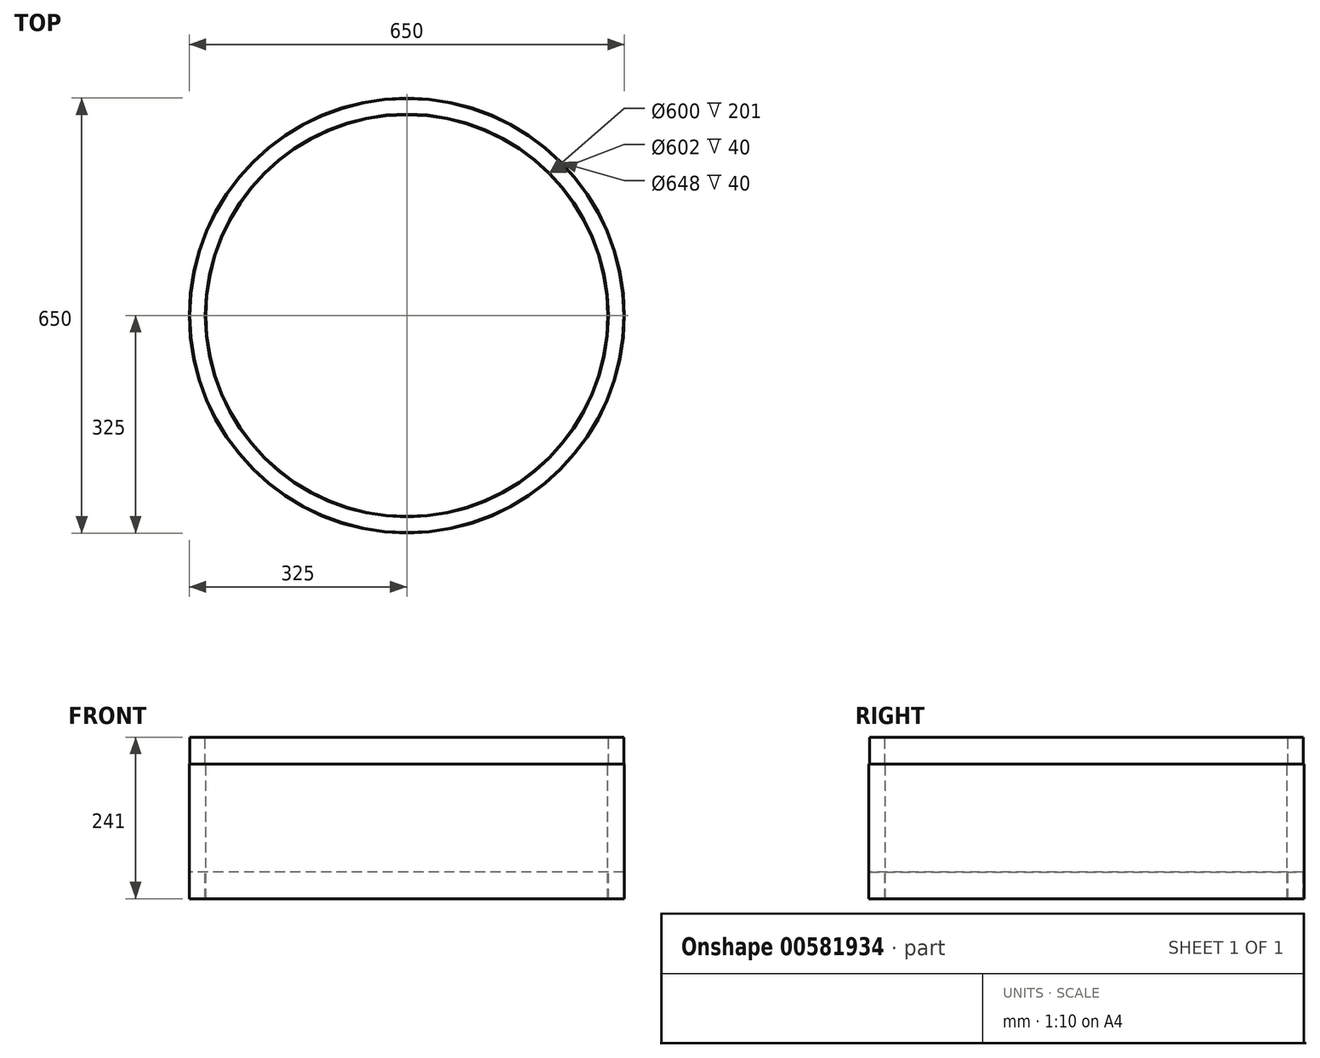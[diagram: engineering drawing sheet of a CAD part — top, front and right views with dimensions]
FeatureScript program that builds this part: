
annotation { "Feature Type Name" : "Feature", "Feature Type Description" : "" }
export const myFeature = defineFeature(function(context is Context, id is Id, definition is map)
    precondition{}
    {
        {
            var Q0;
            Q0=qCreatedBy(makeId("Front.planeOp"),FACE);
            var sketch = newSketch(context, id + "F0", { "sketchPlane" : qUnion([Q0])});
            skLineSegment(sketch, "E0", {"start": v(0, 345.75) * mm, "end": v(0, -558.03) * mm, "construction": true});
            skLineSegment(sketch, "E1", {"start": v(-300, -518.84) * mm, "end": v(-300, -317.84) * mm});
            skLineSegment(sketch, "E2", {"start": v(-300, -317.84) * mm, "end": v(-301, -317.84) * mm});
            skLineSegment(sketch, "E3", {"start": v(-301, -317.84) * mm, "end": v(-301, -277.84) * mm});
            skLineSegment(sketch, "E4", {"start": v(-301, -277.84) * mm, "end": v(-324, -277.84) * mm});
            skLineSegment(sketch, "E5", {"start": v(-324, -277.84) * mm, "end": v(-324, -317.84) * mm});
            skLineSegment(sketch, "E6", {"start": v(-324, -317.84) * mm, "end": v(-325, -317.84) * mm});
            skLineSegment(sketch, "E7", {"start": v(-325, -317.84) * mm, "end": v(-325, -518.84) * mm});
            skLineSegment(sketch, "E8", {"start": v(-325, -518.84) * mm, "end": v(-324, -518.84) * mm});
            skLineSegment(sketch, "E9", {"start": v(-324, -518.84) * mm, "end": v(-324, -478.84) * mm});
            skLineSegment(sketch, "E10", {"start": v(-324, -478.84) * mm, "end": v(-301, -478.84) * mm});
            skLineSegment(sketch, "E11", {"start": v(-301, -478.84) * mm, "end": v(-301, -518.84) * mm});
            skLineSegment(sketch, "E12", {"start": v(-301, -518.84) * mm, "end": v(-300, -518.84) * mm});
            skSolve(sketch);
        }
        {
            var Q0;
            Q0=qSketchRegion(id+"F0",true);
            var Q1;
            Q1=sQuery(id+"F0.wireOp",EDGE,"E0");
            revolve(context, id + "F1", {"entities" : qUnion([Q0]), "axis" : qUnion([Q1]), "revolveType" : RevolveType.FULL});
        }
    });
